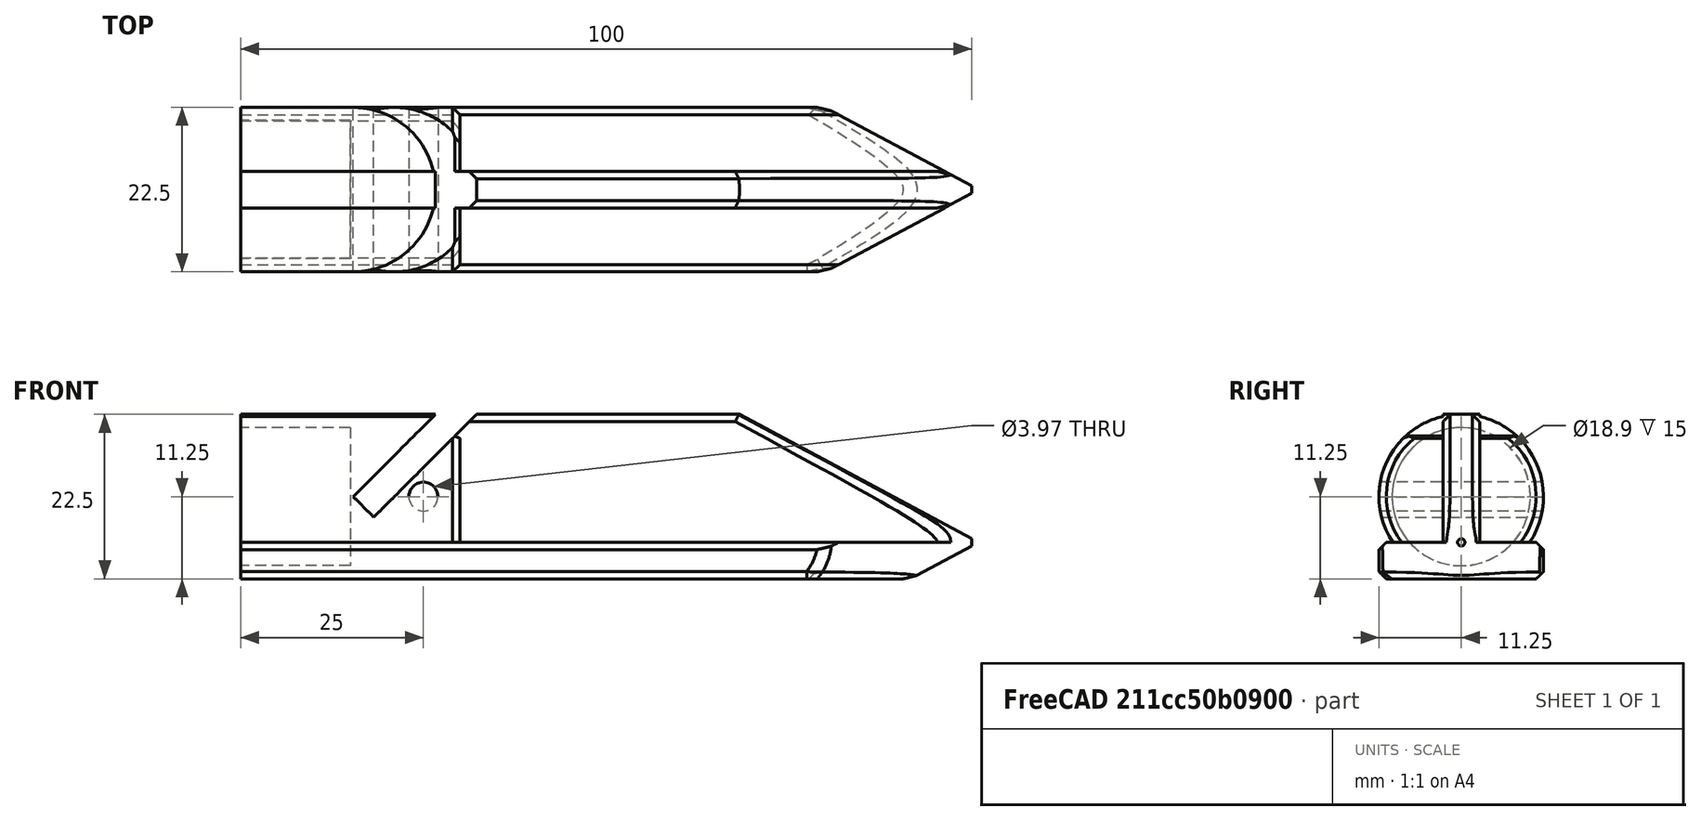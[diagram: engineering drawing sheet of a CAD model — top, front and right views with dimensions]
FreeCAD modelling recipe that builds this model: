
FCSTD DOCUMENT  (FreeCAD 0.18R16117 (Git))
Label: glow_stake
License: All rights reserved
LicenseURL: http://en.wikipedia.org/wiki/All_rights_reserved
objects: Part::Chamfer×4, Part::Box×3, Part::Cylinder×3, Part::Cut×3, Spreadsheet::Sheet×1, Part::Cone×1, Part::MultiFuse×1, Part::MultiCommon×1
note: 16 computed .brp shape members not serialized (recipe doc carries the construction recipe); baked Part::Feature solids carry a one-line shape summary decoded from their .brp

FEATURE [Part::Box] Box  label="Cube"
  AttacherType = Attacher::AttachEngine3D
  Height = 5
  Length = 100
  Width = 22.5
  expr: Height = Spreadsheet.stake_thickness
  expr: Width = Spreadsheet.stake_width
  expr: Length = Spreadsheet.stake_length
FEATURE [Spreadsheet::Sheet] Spreadsheet
  cells = A1=stake_length; B1(stake_length)==100mm; A2=stake_width; B2(stake_width)==22.5mm; A3=stake_thicknes; B3(stake_thickness)==5mm; A4=head_height; B4(head_height)==30mm; A5=head_hole_height; B5(head_hole_height)==15mm; A6=head_wall_thickness; B6(head_wall_thickness)==1.8mm
FEATURE [Part::Box] Box001  label="Cube001"
  AttacherType = Attacher::AttachEngine3D
  Height = 5
  Length = 100
  Placement = pos=(0,13.75,5) rot=(1,0,0;1.5708rad)
  Width = 17.5
  expr: Placement.Base.y = Spreadsheet.stake_width / 2 + Spreadsheet.stake_thickness / 2
  expr: Placement.Base.z = Spreadsheet.stake_thickness
  expr: Height = Spreadsheet.stake_thickness
  expr: Width = Spreadsheet.stake_width - Spreadsheet.stake_thickness
  expr: Length = Spreadsheet.stake_length
FEATURE [Part::Cylinder] Cylinder  label="head"
  Angle = 360
  AttacherType = Attacher::AttachEngine3D
  Height = 30
  Placement = pos=(30,11.25,11.25) rot=(0,1,0;4.71239rad)
  Radius = 11.25
  expr: Height = Spreadsheet.head_height
  expr: Placement.Base.z = Spreadsheet.stake_width / 2
  expr: Radius = Spreadsheet.stake_width / 2
  expr: Placement.Base.x = Spreadsheet.head_height
  expr: Placement.Base.y = Spreadsheet.stake_width / 2
FEATURE [Part::Cylinder] Cylinder001  label="head_socket"
  Angle = 360
  AttacherType = Attacher::AttachEngine3D
  Height = 15
  Placement = pos=(15,11.25,11.25) rot=(0,1,0;4.71239rad)
  Radius = 9.45
  expr: Height = Spreadsheet.head_hole_height
  expr: Placement.Base.z = Spreadsheet.stake_width / 2
  expr: Radius = Spreadsheet.stake_width / 2 - Spreadsheet.head_wall_thickness
  expr: Placement.Base.x = Spreadsheet.head_height - Spreadsheet.head_hole_height
  expr: Placement.Base.y = Spreadsheet.stake_width / 2
FEATURE [Part::Cone] Cone
  Angle = 360
  AttacherType = Attacher::AttachEngine3D
  Height = 100
  Placement = pos=(100,11.25,5) rot=(0,-1,0;1.5708rad)
  Radius1 = 0.500126
  Radius2 = 54
  expr: Placement.Base.z = Spreadsheet.stake_thickness
  expr: Height = Spreadsheet.stake_length
  expr: Radius2 = Spreadsheet.stake_width / 1.25 * 3
  expr: Placement.Base.y = Spreadsheet.stake_width / 2
  expr: Placement.Base.x = Spreadsheet.stake_length
FEATURE [Part::MultiFuse] Fusion
  Shapes = -> [Box,Box001,Cylinder]
FEATURE [Part::Cut] Cut
  Base = -> Fusion
  Tool = -> Cylinder001
FEATURE [Part::MultiCommon] Common
  Shapes = -> [Cut,Cone]
FEATURE [Part::Cylinder] Cylinder002  label="Cylinder"
  Angle = 360
  AttacherType = Attacher::AttachEngine3D
  Height = 22.5
  Placement = pos=(25,22.5,11.25) rot=(1,0,0;1.5708rad)
  Radius = 1.98438
  expr: Placement.Base.z = Spreadsheet.stake_width / 2
  expr: Height = Spreadsheet.stake_width
  expr: Placement.Base.y = Spreadsheet.stake_width
  expr: Placement.Base.x = Spreadsheet.head_height - Spreadsheet.head_hole_height / 3
FEATURE [Part::Box] Box002  label="Cube002"
  AttacherType = Attacher::AttachEngine3D
  Height = 25.4
  Length = 3.96875
  Placement = pos=(15.4,0,11.25) rot=(0,1,0;0.785398rad)
  Width = 22.5
  expr: Placement.Base.x = Spreadsheet.head_hole_height + 0.4mm
  expr: Placement.Base.z = Spreadsheet.stake_width / 2
  expr: Width = Spreadsheet.stake_width
FEATURE [Part::Cut] Cut001
  Base = -> Common
  Tool = -> Cylinder002
FEATURE [Part::Cut] Cut002
  Base = -> Cut001
  Tool = -> Box002
FEATURE [Part::Chamfer] Chamfer
  Base = -> Cut002
  Edges = 2 edges r=1: [Edge24,Edge27]
FEATURE [Part::Chamfer] Chamfer001
  Base = -> Chamfer
  Edges = 8 edges r=1: [Edge8,Edge9,Edge26,Edge27,Edge40,Edge41,Edge55,Edge57]
FEATURE [Part::Chamfer] Chamfer002
  Base = -> Chamfer001
  Edges = 1 edges r=1: [Edge19]
FEATURE [Part::Chamfer] Chamfer003
  Base = -> Chamfer002
  Edges = 4 edges r=1: [Edge65,Edge75,Edge86,Edge92]
